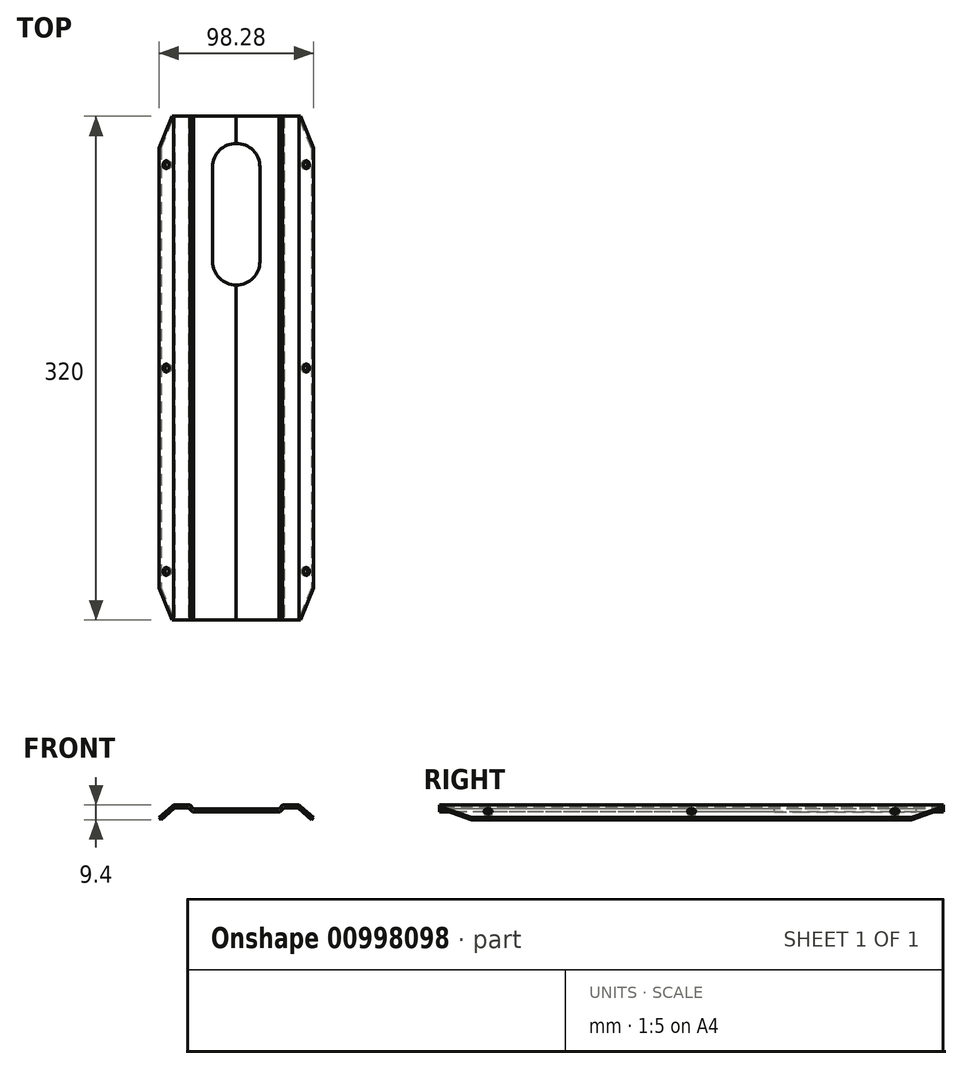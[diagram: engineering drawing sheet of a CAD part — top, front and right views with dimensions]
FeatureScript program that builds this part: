
annotation { "Feature Type Name" : "Feature", "Feature Type Description" : "" }
export const myFeature = defineFeature(function(context is Context, id is Id, definition is map)
    precondition{}
    {
        {
            var Q0;
            Q0=qCreatedBy(makeId("Front.planeOp"),FACE);
            var sketch = newSketch(context, id + "F0", { "sketchPlane" : qUnion([Q0])});
            skLineSegment(sketch, "E0.MirrorCS", {"start": v(-40, -5.5) * mm, "end": v(-49.14, -13.42) * mm});
            skLineSegment(sketch, "E1", {"start": v(0, -293.98) * mm, "end": v(0, 32.01) * mm, "construction": true});
            skLineSegment(sketch, "E2", {"start": v(-40, -5.5) * mm, "end": v(-29.47, -5.5) * mm});
            skLineSegment(sketch, "E3", {"start": v(-27.8, -9.95) * mm, "end": v(0, -9.95) * mm});
            skLineSegment(sketch, "E4", {"start": v(-27.02, -7.95) * mm, "end": v(0, -7.95) * mm});
            skLineSegment(sketch, "E5", {"start": v(-30.25, -7.5) * mm, "end": v(-39.25, -7.5) * mm});
            skLineSegment(sketch, "E6", {"start": v(-47.8, -14.9) * mm, "end": v(-39.25, -7.5) * mm});
            skLineSegment(sketch, "E7", {"start": v(-49.14, -13.42) * mm, "end": v(-47.8, -14.9) * mm});
            skLineSegment(sketch, "E8", {"start": v(-29.47, -5.5) * mm, "end": v(-27.02, -7.95) * mm});
            skLineSegment(sketch, "E9", {"start": v(-30.25, -7.5) * mm, "end": v(-27.8, -9.95) * mm});
            skLineSegment(sketch, "E10", {"start": v(0, -7.95) * mm, "end": v(0, -9.95) * mm});
            skSolve(sketch);
        }
        {
            var Q0;
            Q0=qCreatedBy(makeId("Right.planeOp"),FACE);
            var sketch = newSketch(context, id + "F1", { "sketchPlane" : qUnion([Q0])});
            skLineSegment(sketch, "E11", {"start": v(0, 0) * mm, "end": v(260, 0) * mm});
            skLineSegment(sketch, "E12", {"start": v(260, 28.78) * mm, "end": v(260, -19.4) * mm, "construction": true});
            skLineSegment(sketch, "E13", {"start": v(212.2, 0) * mm, "end": v(0, 0) * mm});
            skSolve(sketch);
        }
        {
            var Q0;
            Q0=makeQuery(id+"F0.imprint","IMPRINT",FACE,{"disambiguationData":[TD([[makeQuery(id+"F0.imprint","IMPRINT",EDGE,{"derivedFrom":sQuery(id+"F0.wireOp",EDGE,"E0.MirrorCS")}),1.0]])]});
            extrude(context, id + "F2", {"entities" : qUnion([Q0]), "oppositeDirection" : true, "depth" : 320 * mm, "offsetDistance" : 25.4 * mm});
        }
        {
            var Q0;
            Q0=makeQuery(id+"F2.opExtrude","SWEPT_FACE",FACE,{"disambiguationData":[OSD([sQuery(id+"F0.wireOp",EDGE,"E0.MirrorCS")])]});
            var sketch = newSketch(context, id + "F3", { "sketchPlane" : qUnion([Q0])});
            skPoint(sketch, "E14", {"position": v(-39.9, 30.83) * mm});
            skPoint(sketch, "E15.0.1.0", {"position": v(-39.9, 160) * mm});
            skPoint(sketch, "E15.0.2.0", {"position": v(-39.9, 289.17) * mm});
            skLineSegment(sketch, "E15.direction1", {"start": v(-39.9, 30.83) * mm, "end": v(-27.68, 30.83) * mm, "construction": true});
            skLineSegment(sketch, "E15.direction2", {"start": v(-39.9, 30.83) * mm, "end": v(-39.9, 160) * mm, "construction": true});
            skLineSegment(sketch, "E16", {"start": v(-39.9, 320) * mm, "end": v(-39.9, 0) * mm, "construction": true});
            skSolve(sketch);
        }
        {
            var Q0;
            Q0=sQuery(id+"F3.wireOp",VERTEX,"E15.0.2.0");
            var Q1;
            Q1=sQuery(id+"F3.wireOp",VERTEX,"E15.0.1.0");
            var Q2;
            Q2=sQuery(id+"F3.wireOp",VERTEX,"E14");
            var Q3;
            Q3=makeQuery(id+"F2.opExtrude","SWEPT_BODY",BODY,{"disambiguationData":[OSD([sQuery(id+"F0.wireOp",EDGE,"E0.MirrorCS"),sQuery(id+"F0.wireOp",EDGE,"2TKtJtls-HKZL-9pNc-KhSM-2cr5P1jvKiuO"),sQuery(id+"F0.wireOp",EDGE,"E2"),sQuery(id+"F0.wireOp",EDGE,"fDTOxo3d-3rfX-dBY2-zsrn-CqeZibWQkMEg"),sQuery(id+"F0.wireOp",EDGE,"E3"),sQuery(id+"F0.wireOp",EDGE,"5IlnrrRk-z5Vu-BmW8-36St-VWP8HLIqOyHw"),sQuery(id+"F0.wireOp",EDGE,"E4"),sQuery(id+"F0.wireOp",EDGE,"E5"),sQuery(id+"F0.wireOp",EDGE,"ODpkLtvZ-vErJ-WUVO-MY3c-zyF2DTRlXPyZ"),sQuery(id+"F0.wireOp",EDGE,"4b80dda3-bf22-4c31-a00e-16da6902330a0.MirrorCS"),sQuery(id+"F0.wireOp",EDGE,"4b80dda3-bf22-4c31-a00e-16da6902330a1.MirrorCS"),sQuery(id+"F0.wireOp",EDGE,"4b80dda3-bf22-4c31-a00e-16da6902330a2.MirrorCS"),sQuery(id+"F0.wireOp",EDGE,"4b80dda3-bf22-4c31-a00e-16da6902330a3.MirrorCS"),sQuery(id+"F0.wireOp",EDGE,"4b80dda3-bf22-4c31-a00e-16da6902330a4.MirrorCS"),sQuery(id+"F0.wireOp",EDGE,"4b80dda3-bf22-4c31-a00e-16da6902330a5.MirrorCS"),sQuery(id+"F0.wireOp",EDGE,"4b80dda3-bf22-4c31-a00e-16da6902330a6.MirrorCS"),sQuery(id+"F0.wireOp",EDGE,"4b80dda3-bf22-4c31-a00e-16da6902330a7.MirrorCS"),sQuery(id+"F0.wireOp",EDGE,"4b80dda3-bf22-4c31-a00e-16da6902330a8.MirrorCS")])]});
            hole(context, id + "F4", {"style" : HoleStyle.SIMPLE, "endStyle" : HoleEndStyle.THROUGH, "holeDiameter" : 5 * mm, "majorDiameter" : 6.35 * mm, "isTappedThrough" : true, "tappedDepth" : 12.7 * mm, "tapClearance" : 3, "locations" : qUnion([Q0, Q1, Q2]), "scope" : qUnion([Q3])});
        }
        {
            var Q0;
            Q0=makeQuery(id+"F2.opExtrude","SWEPT_FACE",FACE,{"disambiguationData":[OSD([sQuery(id+"F0.wireOp",EDGE,"E4"),sQuery(id+"F0.wireOp",EDGE,"4b80dda3-bf22-4c31-a00e-16da6902330a1.MirrorCS")])]});
            var sketch = newSketch(context, id + "F5", { "sketchPlane" : qUnion([Q0])});
            skLineSegment(sketch, "E17", {"start": v(-15, 287.71) * mm, "end": v(-15, 227.71) * mm});
            skLineSegment(sketch, "E18.MirrorCS", {"start": v(15, 287.71) * mm, "end": v(15, 227.71) * mm});
            skArc(sketch, "E19", {"start": v(15, 287.71) * mm, "mid": v(0, 302.71) * mm, "end": v(-15, 287.71) * mm});
            skArc(sketch, "E20", {"start": v(-15, 227.71) * mm, "mid": v(0, 212.71) * mm, "end": v(15, 227.71) * mm});
            skSolve(sketch);
        }
        {
            var Q0;
            Q0=makeQuery(id+"F5.imprint","IMPRINT",FACE,{"disambiguationData":[TD([[makeQuery(id+"F5.imprint","IMPRINT",EDGE,{"derivedFrom":sQuery(id+"F5.wireOp",EDGE,"E17")}),1.0]])]});
            extrude(context, id + "F6", {"entities" : qUnion([Q0]), "operationType" : NewBodyOperationType.REMOVE, "endBound" : BoundingType.THROUGH_ALL, "oppositeDirection" : true, "depth" : 25.4 * mm, "offsetDistance" : 25.4 * mm});
        }
        {
            var Q0;
            Q0=makeQuery(id+"F2.opExtrude","SWEPT_FACE",FACE,{"disambiguationData":[OSD([sQuery(id+"F0.wireOp",EDGE,"E0.MirrorCS")])]});
            var sketch = newSketch(context, id + "F7", { "sketchPlane" : qUnion([Q0])});
            skLineSegment(sketch, "E21", {"start": v(-35.03, 320) * mm, "end": v(-45.94, 299.7) * mm});
            skLineSegment(sketch, "E22", {"start": v(-35.03, 0) * mm, "end": v(-45.94, 20.3) * mm});
            skSolve(sketch);
        }
        {
            var Q0;
            {var subQ0=sQuery(id+"F7.wireOp",EDGE,"E21");Q0=makeQuery(id+"F7.imprint","IMPRINT",FACE,{"disambiguationData":[TD([[makeQuery(id+"F7.imprint","IMPRINT",EDGE,{"derivedFrom":subQ0}),-1.0]])]});}
            var Q1;
            {var subQ0=sQuery(id+"F0.wireOp",EDGE,"E0.MirrorCS");var subQ1=makeQuery(id+"F2.opExtrude","CAP_EDGE",EDGE,{"disambiguationData":[OSD([subQ0])],"isStart":true});var subQ4=sQuery(id+"F7.wireOp",EDGE,"E22");var subQ5=makeQuery(id+"F7.imprint","INTERSECT",VERTEX,{"derivedFrom":[subQ1,subQ4]});Q1=makeQuery(id+"F7.imprint","IMPRINT",FACE,{"disambiguationData":[TD([[makeQuery(id+"F7.imprint","IMPRINT",EDGE,{"disambiguationData":[TD([[subQ5,-1.0]])],"derivedFrom":subQ4}),1.0]])]});}
            extrude(context, id + "F8", {"entities" : qUnion([Q0, Q1]), "operationType" : NewBodyOperationType.REMOVE, "endBound" : BoundingType.THROUGH_ALL, "oppositeDirection" : true, "depth" : 25.4 * mm, "offsetDistance" : 25.4 * mm});
        }
        {
            var Q0;
            Q0=sQuery(id+"F1.wireOp",VERTEX,"E11.end");
            var Q1;
            Q1=sQuery(id+"F1.wireOp",VERTEX,"E12.start");
            var Q2;
            Q2=sQuery(id+"F1.wireOp",VERTEX,"E11.start");
            cPlane(context, id + "F9", {"entities" : qUnion([Q0, Q1, Q2]), "cplaneType" : CPlaneType.THREE_POINT, "offset" : 25.4 * mm, "width" : 152.4 * mm, "height" : 152.4 * mm});
        }
        {
            var Q0;
            Q0=makeQuery(id+"F2.opExtrude","SWEPT_BODY",BODY,{"disambiguationData":[OSD([sQuery(id+"F0.wireOp",EDGE,"E0.MirrorCS"),sQuery(id+"F0.wireOp",EDGE,"E2"),sQuery(id+"F0.wireOp",EDGE,"E3"),sQuery(id+"F0.wireOp",EDGE,"E4"),sQuery(id+"F0.wireOp",EDGE,"E5"),sQuery(id+"F0.wireOp",EDGE,"E6"),sQuery(id+"F0.wireOp",EDGE,"E7"),sQuery(id+"F0.wireOp",EDGE,"E8"),sQuery(id+"F0.wireOp",EDGE,"E9"),sQuery(id+"F0.wireOp",EDGE,"E10")])]});
            var Q1;
            Q1=qCreatedBy(id+"F9.planeOp",FACE);
            mirror(context, id + "F10", {"entities" : qUnion([Q0]), "mirrorPlane" : qUnion([Q1])});
        }
    });
